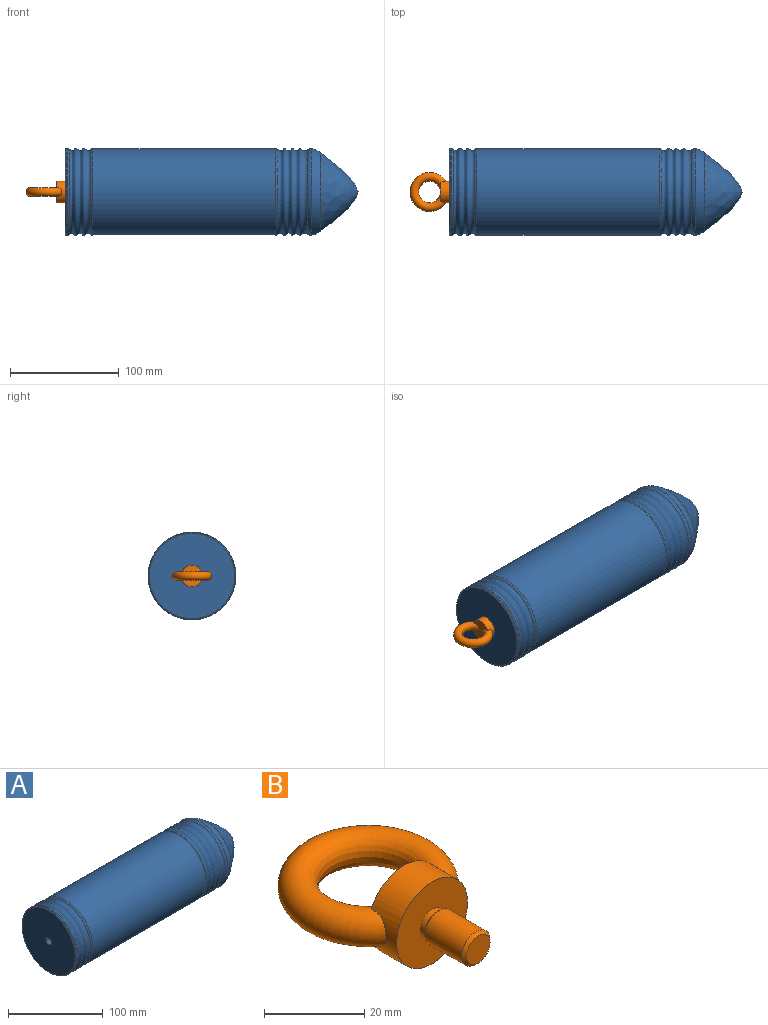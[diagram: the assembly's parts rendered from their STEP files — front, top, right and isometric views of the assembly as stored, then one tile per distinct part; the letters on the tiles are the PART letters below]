
ASSEMBLY  parts=2 mates=1
PART A: 15 faces, bbox 237.6x87.8x87.8 mm
  f0: revolved ~79.98x79.98mm, area 7675.7mm2, adj f1,f4
  f1: torus R=33.14mm, axis (-1,0,0), area 822.5mm2, adj f0,f2
  f2: cone r=40.13mm half-angle=4deg, axis (1,0,0), area 28.7mm2, adj f1,f3
  f3: torus R=20.54mm, axis (-1,0,0), area 2208.9mm2, adj f2
  f4: torus R=37mm, axis (-1,0,0), area 578.6mm2, adj f0,f5
  f5: cylinder r=40mm len=168.45mm, axis (-1,0,0), area 42336.1mm2, adj f4,f6
  f6: torus R=37mm, axis (-1,0,0), area 602.2mm2, adj f5,f7
  f7: revolved ~80.65x80.65mm, area 5681.8mm2, adj f6,f8
  f8: torus R=37.32mm, axis (-1,0,0), area 580.4mm2, adj f7,f9
  f9: cylinder r=40.32mm len=80.65mm, axis (-1,0,0), area 204.4mm2, adj f8,f10
  f10: torus R=39.32mm, axis (-1,0,0), area 394.4mm2, adj f9,f11
  f11: plane 78.65x78.65mm, normal (-1,0,0), area 4807.6mm2, adj f10,f12
  f12: cylinder r=4mm len=16mm, axis (-1,0,0), area 402.1mm2, adj f11,f13
  f13: cone r=0mm half-angle=59deg, axis (-1,0,0), area 58.6mm2, adj f12
  f14: revolved ~72.75x36.37mm, area 0mm2
PART B: 10 faces, bbox 39x50.5x20 mm
  f0: torus R=14mm, axis (0,0,1), area 1822.1mm2, adj f1,f2,f4
  f1: plane 18.36x10mm, normal (0,1,0), area 108.2mm2, adj f0,f4
  f2: plane 18.36x10mm, normal (0,1,0), area 108.2mm2, adj f0,f4
  f3: plane 20x20mm, normal (0,-1,0), area 279.5mm2, adj f4,f9
  f4: cylinder r=10mm len=20mm, axis (0,1,0), area 435.4mm2, adj f0,f1,f2,f3
  f5: plane 6.65x6.65mm, normal (0,-1,0), area 34.7mm2, adj f6
  f6: cone r=3.32mm half-angle=45deg, axis (0,1,0), area 22mm2, adj f5,f7
  f7: cylinder r=4mm len=10.35mm, axis (0,-1,0), area 260mm2, adj f6,f8
  f8: cone r=4mm half-angle=45deg, axis (0,-1,0), area 22mm2, adj f7,f9
  f9: cylinder r=3.32mm len=6.65mm, axis (0,-1,0), area 27.1mm2, adj f3,f8
PLACE A t=(170.67,66.8,-47.6)mm
PLACE B rot(axis=(0,0,1),90deg) t=(13.24,66.8,-47.6)mm
MATE fastened B.f4 <-> A.f5  axis (1,0,0) through (13.24,66.8,-47.6)mm
